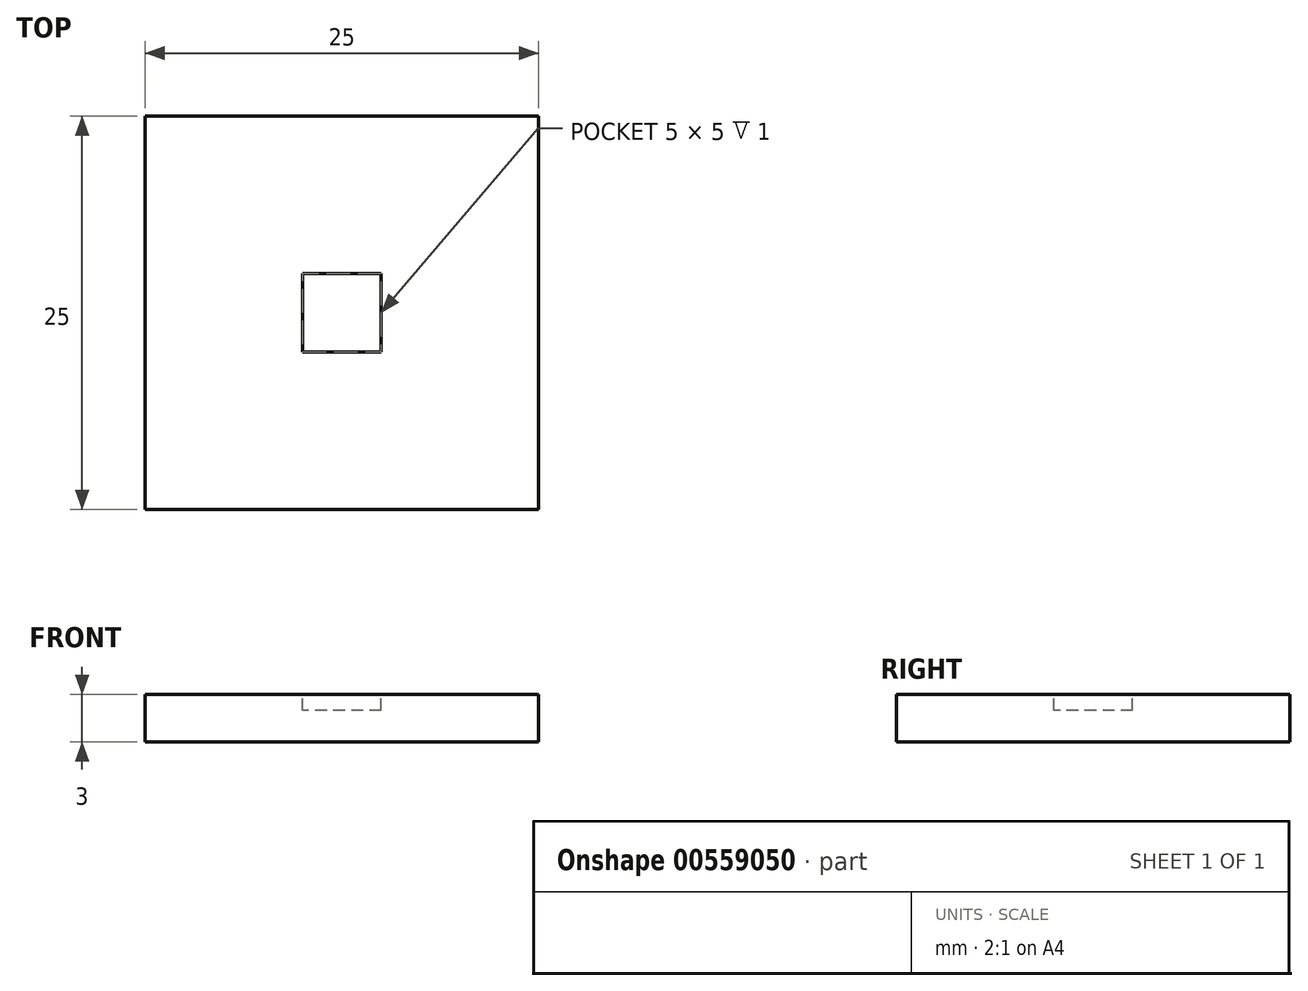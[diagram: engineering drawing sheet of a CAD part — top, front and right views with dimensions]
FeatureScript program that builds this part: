
annotation { "Feature Type Name" : "Feature", "Feature Type Description" : "" }
export const myFeature = defineFeature(function(context is Context, id is Id, definition is map)
    precondition{}
    {
        {
            var Q0;
            Q0=qCreatedBy(makeId("Top.planeOp"),FACE);
            var sketch = newSketch(context, id + "F0", { "sketchPlane" : qUnion([Q0])});
            skLineSegment(sketch, "E0.bottom", {"start": v(12.5, 12.5) * mm, "end": v(-12.5, 12.5) * mm});
            skLineSegment(sketch, "E0.top", {"start": v(12.5, -12.5) * mm, "end": v(-12.5, -12.5) * mm});
            skLineSegment(sketch, "E0.left", {"start": v(12.5, 12.5) * mm, "end": v(12.5, -12.5) * mm});
            skLineSegment(sketch, "E0.right", {"start": v(-12.5, 12.5) * mm, "end": v(-12.5, -12.5) * mm});
            skSolve(sketch);
        }
        {
            var Q0;
            Q0 = qSketchRegion(id + "F0", true);
            extrude(context, id + "F1", {"entities" : qUnion([Q0]), "depth" : 3 * mm, "offsetDistance" : 25 * mm});
        }
        {
            var Q0;
            Q0=makeQuery(id+"F1.opExtrude","CAP_FACE",FACE,{"disambiguationData":[OSD([sQuery(id+"F0.wireOp",EDGE,"E0.bottom"),sQuery(id+"F0.wireOp",EDGE,"E0.top"),sQuery(id+"F0.wireOp",EDGE,"E0.left"),sQuery(id+"F0.wireOp",EDGE,"E0.right")])],"isStart":false});
            var sketch = newSketch(context, id + "F2", { "sketchPlane" : qUnion([Q0])});
            skLineSegment(sketch, "E1.bottom", {"start": v(2.5, 2.5) * mm, "end": v(-2.5, 2.5) * mm});
            skLineSegment(sketch, "E1.top", {"start": v(2.5, -2.5) * mm, "end": v(-2.5, -2.5) * mm});
            skLineSegment(sketch, "E1.left", {"start": v(2.5, 2.5) * mm, "end": v(2.5, -2.5) * mm});
            skLineSegment(sketch, "E1.right", {"start": v(-2.5, 2.5) * mm, "end": v(-2.5, -2.5) * mm});
            skPoint(sketch, "E1.middle", {"position": v(0, 0) * mm});
            skSolve(sketch);
        }
        {
            var Q0;
            Q0=makeQuery(id+"F2.imprint","IMPRINT",FACE,{"disambiguationData":[TD([[makeQuery(id+"F2.imprint","IMPRINT",EDGE,{"derivedFrom":sQuery(id+"F2.wireOp",EDGE,"E1.bottom")}),1.0]])]});
            extrude(context, id + "F3", {"entities" : qUnion([Q0]), "depth" : -1 * mm, "offsetDistance" : 25 * mm});
        }
        {
            var Q0;
            Q0=makeQuery(id+"F3.opExtrude","SWEPT_BODY",BODY,{"disambiguationData":[OSD([sQuery(id+"F2.wireOp",EDGE,"E1.bottom"),sQuery(id+"F2.wireOp",EDGE,"E1.top"),sQuery(id+"F2.wireOp",EDGE,"E1.left"),sQuery(id+"F2.wireOp",EDGE,"E1.right")])]});
            var Q1;
            Q1=makeQuery(id+"F1.opExtrude","SWEPT_BODY",BODY,{"disambiguationData":[OSD([sQuery(id+"F0.wireOp",EDGE,"E0.bottom"),sQuery(id+"F0.wireOp",EDGE,"E0.top"),sQuery(id+"F0.wireOp",EDGE,"E0.left"),sQuery(id+"F0.wireOp",EDGE,"E0.right")])]});
            booleanBodies(context, id + "F4", {"operationType" : BooleanOperationType.SUBTRACTION, "tools" : qUnion([Q0]), "targets" : qUnion([Q1])});
        }
    });
